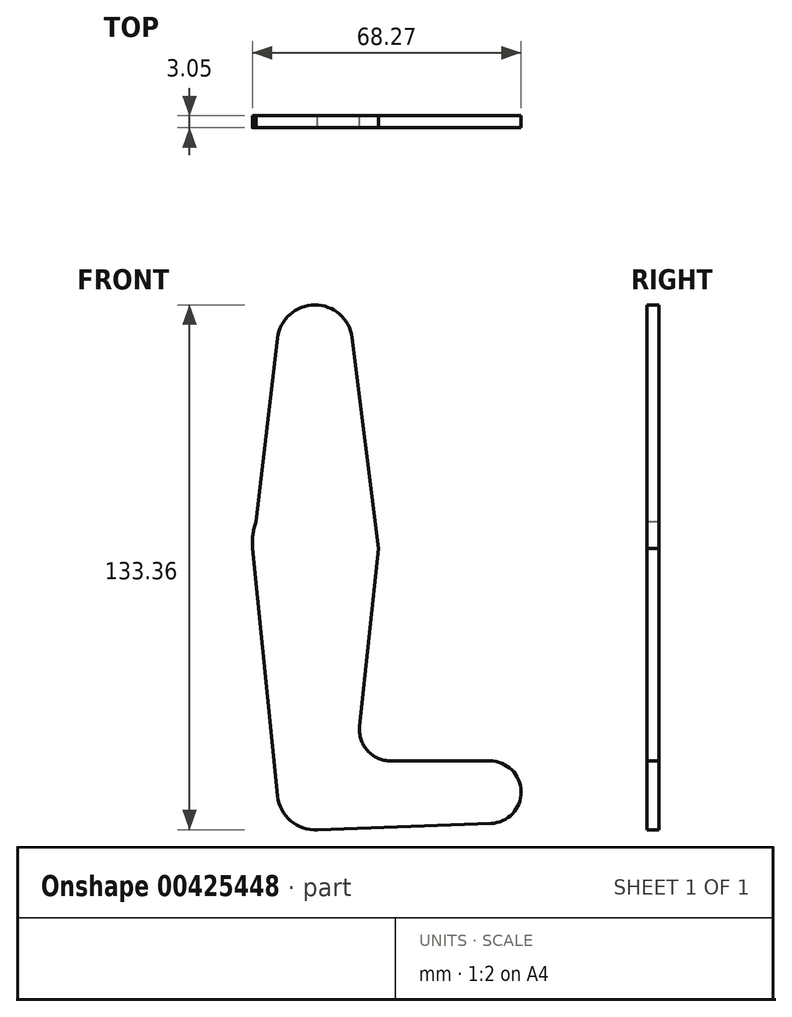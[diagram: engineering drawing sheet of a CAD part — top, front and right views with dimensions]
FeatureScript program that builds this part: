
annotation { "Feature Type Name" : "Feature", "Feature Type Description" : "" }
export const myFeature = defineFeature(function(context is Context, id is Id, definition is map)
    precondition{}
    {
        {
            var Q0;
            Q0=qCreatedBy(makeId("Front.planeOp"),FACE);
            var sketch = newSketch(context, id + "F0", { "sketchPlane" : qUnion([Q0])});
            skLineSegment(sketch, "E0", {"start": v(0, 0) * mm, "end": v(0, 114.3) * mm});
            skLineSegment(sketch, "E1", {"start": v(0, 0) * mm, "end": v(44.45, 0) * mm});
            skCircle(sketch, "E2", {"center": v(0, 114.3) * mm, "radius": 9.53 * mm});
            skCircle(sketch, "E3", {"center": v(0, 63.5) * mm, "radius": 15.88 * mm});
            skCircle(sketch, "E4", {"center": v(0, 0) * mm, "radius": 9.53 * mm});
            skCircle(sketch, "E5", {"center": v(44.45, 0) * mm, "radius": 7.94 * mm});
            skLineSegment(sketch, "E6", {"start": v(-9.46, 115.42) * mm, "end": v(-15.8, 61.91) * mm});
            skLineSegment(sketch, "E7", {"start": v(9.45, 115.5) * mm, "end": v(16.2, 61.91) * mm});
            skLineSegment(sketch, "E8", {"start": v(0, -9.52) * mm, "end": v(44.73, -7.93) * mm});
            skLineSegment(sketch, "E9", {"start": v(19.27, 7.94) * mm, "end": v(44.45, 7.94) * mm});
            skLineSegment(sketch, "E10", {"start": v(16.2, 61.91) * mm, "end": v(11.37, 16.73) * mm});
            skArc(sketch, "E11.filletArc", {"start": v(11.37, 16.73) * mm, "mid": v(13.36, 10.57) * mm, "end": v(19.27, 7.94) * mm});
            skLineSegment(sketch, "E12", {"start": v(-15.8, 61.91) * mm, "end": v(-9.48, -0.95) * mm});
            skPoint(sketch, "E13.orphan", {"position": v(-9.57, 0) * mm});
            skSolve(sketch);
        }
        {
            var Q0;
            Q0 = qSketchRegion(id + "F0", true);
            var Q1;
            {var subQ0=sQuery(id+"F0.wireOp",EDGE,"E1");var subQ1=sQuery(id+"F0.wireOp",EDGE,"E0");var subQ2=makeQuery(id+"F0.imprint","INTERSECT",VERTEX,{"derivedFrom":[subQ1,subQ0]});Q1=makeQuery(id+"F0.imprint","IMPRINT",FACE,{"disambiguationData":[TD([[makeQuery(id+"F0.imprint","IMPRINT",EDGE,{"disambiguationData":[TD([[subQ2,-1.0]])],"derivedFrom":subQ1}),-1.0]])]});}
            extrude(context, id + "F1", {"entities" : qUnion([Q0, Q1]), "depth" : 3.05 * mm});
        }
    });
